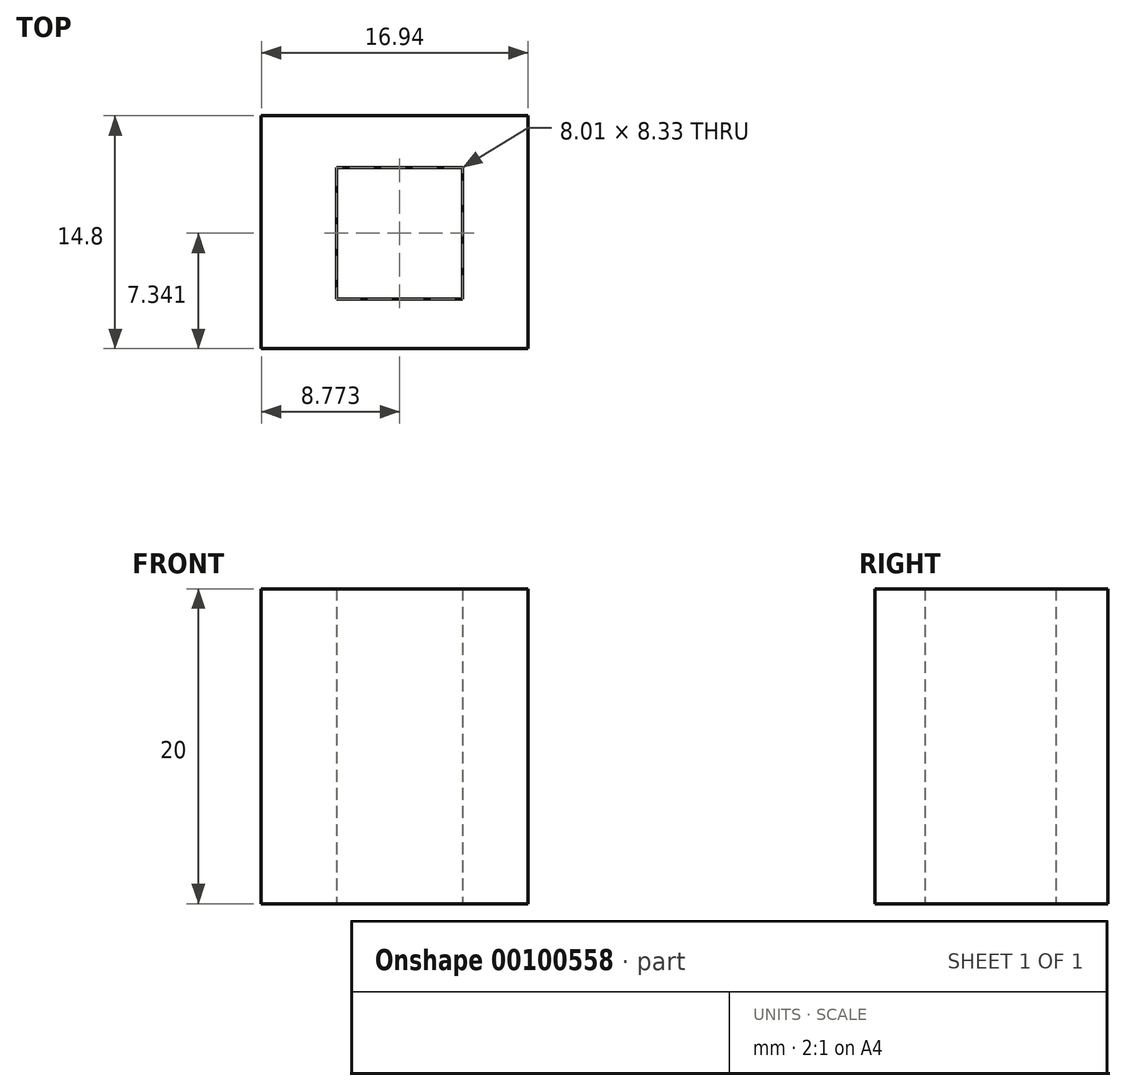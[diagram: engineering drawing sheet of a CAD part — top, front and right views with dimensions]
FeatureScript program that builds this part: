
annotation { "Feature Type Name" : "Feature", "Feature Type Description" : "" }
export const myFeature = defineFeature(function(context is Context, id is Id, definition is map)
    precondition{}
    {
        {
            var Q0;
            Q0=qCreatedBy(makeId("Top.planeOp"),FACE);
            var sketch = newSketch(context, id + "F0", { "sketchPlane" : qUnion([Q0])});
            skLineSegment(sketch, "E0.bottom", {"start": v(-8.47, 7.4) * mm, "end": v(8.48, 7.4) * mm});
            skLineSegment(sketch, "E0.top", {"start": v(-8.48, -7.4) * mm, "end": v(8.47, -7.4) * mm});
            skLineSegment(sketch, "E0.left", {"start": v(-8.47, 7.4) * mm, "end": v(-8.48, -7.4) * mm});
            skLineSegment(sketch, "E0.right", {"start": v(8.48, 7.4) * mm, "end": v(8.47, -7.4) * mm});
            skPoint(sketch, "E0.middle", {"position": v(0, 0) * mm});
            skSolve(sketch);
        }
        {
            var Q0;
            Q0 = qSketchRegion(id + "F0", true);
            extrude(context, id + "F1", {"entities" : qUnion([Q0]), "depth" : 20 * mm});
        }
        {
            var Q0;
            Q0=makeQuery(id+"F1.opExtrude","CAP_FACE",FACE,{"disambiguationData":[OSD([sQuery(id+"F0.wireOp",EDGE,"E0.bottom"),sQuery(id+"F0.wireOp",EDGE,"E0.top"),sQuery(id+"F0.wireOp",EDGE,"E0.left"),sQuery(id+"F0.wireOp",EDGE,"E0.right")])],"isStart":true});
            var sketch = newSketch(context, id + "F2", { "sketchPlane" : qUnion([Q0])});
            skLineSegment(sketch, "E1.bottom", {"start": v(-3.7, 4.23) * mm, "end": v(4.3, 4.23) * mm});
            skLineSegment(sketch, "E1.top", {"start": v(-3.7, -4.1) * mm, "end": v(4.3, -4.1) * mm});
            skLineSegment(sketch, "E1.left", {"start": v(-3.7, 4.23) * mm, "end": v(-3.7, -4.1) * mm});
            skLineSegment(sketch, "E1.right", {"start": v(4.3, 4.23) * mm, "end": v(4.3, -4.1) * mm});
            skSolve(sketch);
        }
        {
            var Q0;
            Q0 = qSketchRegion(id + "F2", true);
            extrude(context, id + "F3", {"entities" : qUnion([Q0]), "operationType" : NewBodyOperationType.REMOVE, "oppositeDirection" : true, "depth" : 25 * mm});
        }
    });
